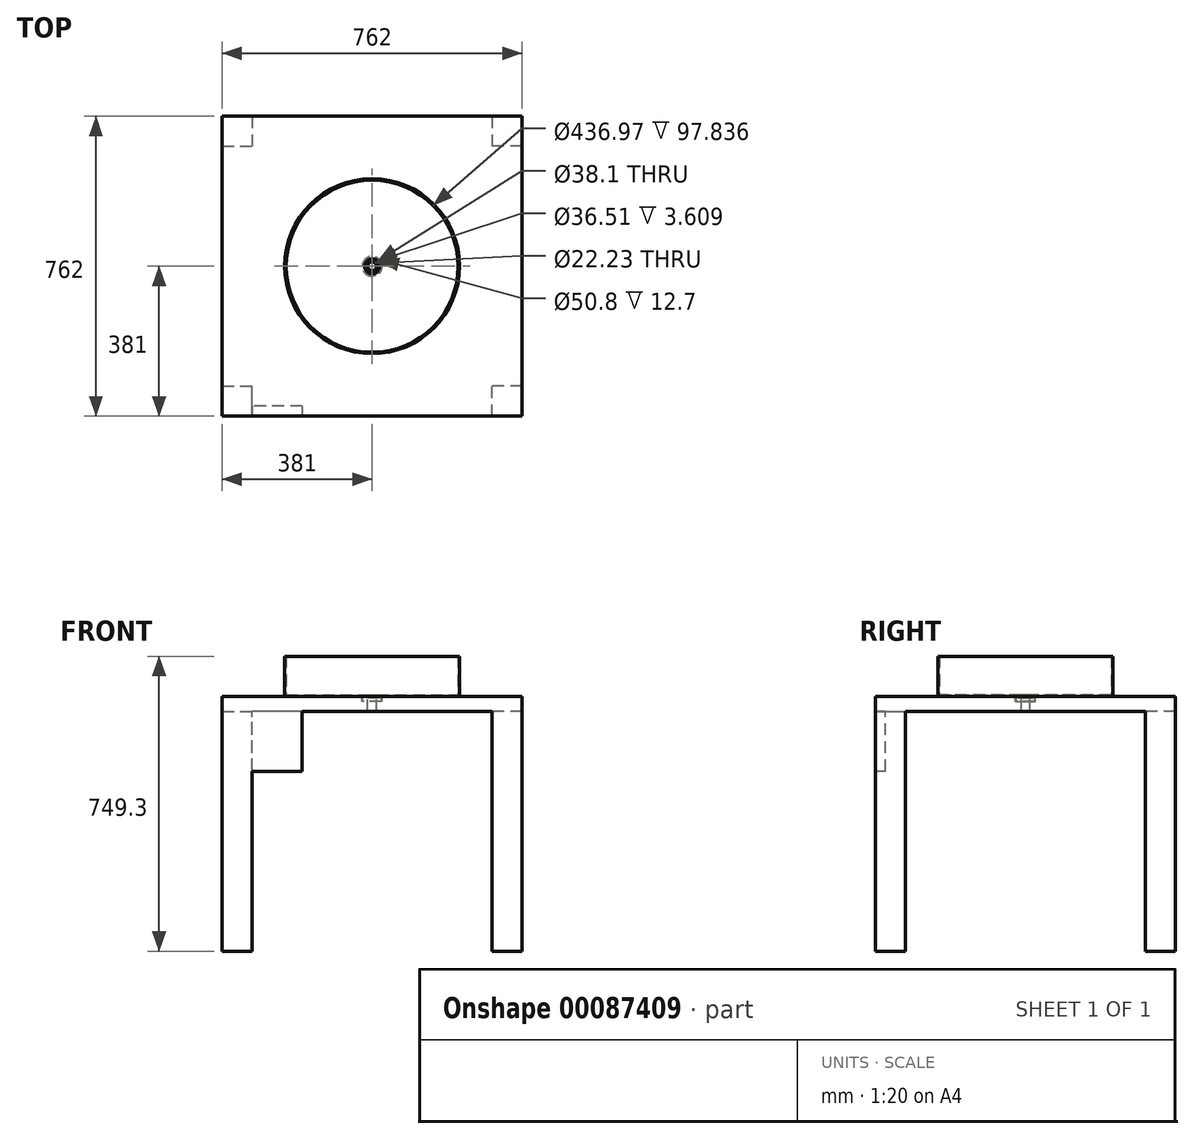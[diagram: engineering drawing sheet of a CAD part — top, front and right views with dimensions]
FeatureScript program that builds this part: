
annotation { "Feature Type Name" : "Feature", "Feature Type Description" : "" }
export const myFeature = defineFeature(function(context is Context, id is Id, definition is map)
    precondition{}
    {
        {
            var Q0;
            Q0=qCreatedBy(makeId("Top.planeOp"),FACE);
            var sketch = newSketch(context, id + "F0", { "sketchPlane" : qUnion([Q0])});
            skLineSegment(sketch, "E0.bottom", {"start": v(381, 381) * mm, "end": v(-381, 381) * mm});
            skLineSegment(sketch, "E0.top", {"start": v(381, -381) * mm, "end": v(-381, -381) * mm});
            skLineSegment(sketch, "E0.left", {"start": v(381, 381) * mm, "end": v(381, -381) * mm});
            skLineSegment(sketch, "E0.right", {"start": v(-381, 381) * mm, "end": v(-381, -381) * mm});
            skPoint(sketch, "E0.middle", {"position": v(0, 0) * mm});
            skSolve(sketch);
        }
        {
            var Q0;
            Q0 = qSketchRegion(id + "F0", true);
            extrude(context, id + "F1", {"entities" : qUnion([Q0]), "depth" : 38.1 * mm});
        }
        {
            var Q0;
            Q0=makeQuery(id+"F1.opExtrude","CAP_FACE",FACE,{"disambiguationData":[OSD([sQuery(id+"F0.wireOp",EDGE,"E0.bottom"),sQuery(id+"F0.wireOp",EDGE,"E0.top"),sQuery(id+"F0.wireOp",EDGE,"E0.left"),sQuery(id+"F0.wireOp",EDGE,"E0.right")])],"isStart":true});
            var sketch = newSketch(context, id + "F2", { "sketchPlane" : qUnion([Q0])});
            skLineSegment(sketch, "E1.bottom", {"start": v(-381, 381) * mm, "end": v(-304.8, 381) * mm});
            skLineSegment(sketch, "E1.top", {"start": v(-381, 304.8) * mm, "end": v(-304.8, 304.8) * mm});
            skLineSegment(sketch, "E1.left", {"start": v(-381, 381) * mm, "end": v(-381, 304.8) * mm});
            skLineSegment(sketch, "E1.right", {"start": v(-304.8, 381) * mm, "end": v(-304.8, 304.8) * mm});
            skLineSegment(sketch, "E2.bottom", {"start": v(381, 381) * mm, "end": v(304.8, 381) * mm});
            skLineSegment(sketch, "E2.top", {"start": v(381, 304.8) * mm, "end": v(304.8, 304.8) * mm});
            skLineSegment(sketch, "E2.left", {"start": v(381, 381) * mm, "end": v(381, 304.8) * mm});
            skLineSegment(sketch, "E2.right", {"start": v(304.8, 381) * mm, "end": v(304.8, 304.8) * mm});
            skLineSegment(sketch, "E3.bottom", {"start": v(381, -381) * mm, "end": v(304.8, -381) * mm});
            skLineSegment(sketch, "E3.top", {"start": v(381, -304.8) * mm, "end": v(304.8, -304.8) * mm});
            skLineSegment(sketch, "E3.left", {"start": v(381, -381) * mm, "end": v(381, -304.8) * mm});
            skLineSegment(sketch, "E3.right", {"start": v(304.8, -381) * mm, "end": v(304.8, -304.8) * mm});
            skLineSegment(sketch, "E4.bottom", {"start": v(-381, -381) * mm, "end": v(-304.8, -381) * mm});
            skLineSegment(sketch, "E4.top", {"start": v(-381, -304.8) * mm, "end": v(-304.8, -304.8) * mm});
            skLineSegment(sketch, "E4.left", {"start": v(-381, -381) * mm, "end": v(-381, -304.8) * mm});
            skLineSegment(sketch, "E4.right", {"start": v(-304.8, -381) * mm, "end": v(-304.8, -304.8) * mm});
            skSolve(sketch);
        }
        {
            var Q0;
            Q0 = qSketchRegion(id + "F2", true);
            extrude(context, id + "F3", {"entities" : qUnion([Q0]), "operationType" : NewBodyOperationType.ADD, "depth" : 609.6 * mm});
        }
        {
            var Q0;
            Q0=makeQuery(id+"F1.opExtrude","CAP_FACE",FACE,{"disambiguationData":[OSD([sQuery(id+"F0.wireOp",EDGE,"E0.bottom"),sQuery(id+"F0.wireOp",EDGE,"E0.top"),sQuery(id+"F0.wireOp",EDGE,"E0.left"),sQuery(id+"F0.wireOp",EDGE,"E0.right")])],"isStart":false});
            var sketch = newSketch(context, id + "F4", { "sketchPlane" : qUnion([Q0])});
            skCircle(sketch, "E5", {"center": v(0, 0) * mm, "radius": 18.26 * mm});
            skSolve(sketch);
        }
        {
            var Q0;
            Q0 = qSketchRegion(id + "F4", true);
            extrude(context, id + "F5", {"entities" : qUnion([Q0]), "operationType" : NewBodyOperationType.REMOVE, "oppositeDirection" : true, "depth" : 3.6 * mm});
        }
        {
            var Q0;
            Q0=makeQuery(id+"F5.boolean.opBoolean","COPY",FACE,{"derivedFrom":makeQuery(id+"F5.opExtrude","CAP_FACE",FACE,{"disambiguationData":[OSD([sQuery(id+"F4.wireOp",EDGE,"E5")])],"isStart":false})});
            var sketch = newSketch(context, id + "F6", { "sketchPlane" : qUnion([Q0])});
            skCircle(sketch, "E6", {"center": v(0, 0) * mm, "radius": 11.11 * mm});
            skSolve(sketch);
        }
        {
            var Q0;
            Q0 = qSketchRegion(id + "F6", true);
            extrude(context, id + "F7", {"entities" : qUnion([Q0]), "operationType" : NewBodyOperationType.REMOVE, "endBound" : BoundingType.THROUGH_ALL, "oppositeDirection" : true, "depth" : 25.4 * mm});
        }
        {
            var Q0;
            Q0=makeQuery(id+"F5.boolean.opBoolean","COPY",FACE,{"derivedFrom":makeQuery(id+"F5.opExtrude","CAP_FACE",FACE,{"disambiguationData":[OSD([sQuery(id+"F4.wireOp",EDGE,"E5")])],"isStart":false})});
            var sketch = newSketch(context, id + "F8", { "sketchPlane" : qUnion([Q0])});
            skCircle(sketch, "E7", {"center": v(0, 0) * mm, "radius": 12.7 * mm});
            skSolve(sketch);
        }
        {
            var Q0;
            Q0=makeQuery(id+"F1.opExtrude","CAP_FACE",FACE,{"disambiguationData":[OSD([sQuery(id+"F0.wireOp",EDGE,"E0.bottom"),sQuery(id+"F0.wireOp",EDGE,"E0.top"),sQuery(id+"F0.wireOp",EDGE,"E0.left"),sQuery(id+"F0.wireOp",EDGE,"E0.right")])],"isStart":false});
            var sketch = newSketch(context, id + "F9", { "sketchPlane" : qUnion([Q0])});
            skCircle(sketch, "E8", {"center": v(0, 0) * mm, "radius": 25.4 * mm});
            skCircle(sketch, "E9.0", {"center": v(0, 0) * mm, "radius": 23.81 * mm});
            skSolve(sketch);
        }
        {
            var Q0;
            Q0 = qSketchRegion(id + "F9", true);
            extrude(context, id + "F10", {"entities" : qUnion([Q0]), "operationType" : NewBodyOperationType.REMOVE, "oppositeDirection" : true, "depth" : 12.7 * mm});
        }
        {
            var Q0;
            Q0=makeQuery(id+"F3.boolean.opBoolean","MERGE",FACE,{"derivedFrom":[makeQuery(id+"F1.opExtrude","SWEPT_FACE",FACE,{"disambiguationData":[OSD([sQuery(id+"F0.wireOp",EDGE,"E0.top")])]}),makeQuery(id+"F3.opExtrude","SWEPT_FACE",FACE,{"disambiguationData":[OSD([sQuery(id+"F2.wireOp",EDGE,"E1.bottom")])]}),makeQuery(id+"F3.opExtrude","SWEPT_FACE",FACE,{"disambiguationData":[OSD([sQuery(id+"F2.wireOp",EDGE,"E2.bottom")])]})]});
            var sketch = newSketch(context, id + "F11", { "sketchPlane" : qUnion([Q0])});
            skLineSegment(sketch, "E10.bottom", {"start": v(-304.8, 0) * mm, "end": v(-177.8, 0) * mm});
            skLineSegment(sketch, "E10.top", {"start": v(-304.8, -152.4) * mm, "end": v(-177.8, -152.4) * mm});
            skLineSegment(sketch, "E10.left", {"start": v(-304.8, 0) * mm, "end": v(-304.8, -152.4) * mm});
            skLineSegment(sketch, "E10.right", {"start": v(-177.8, 0) * mm, "end": v(-177.8, -152.4) * mm});
            skSolve(sketch);
        }
        {
            var Q0;
            Q0 = qSketchRegion(id + "F11", true);
            extrude(context, id + "F12", {"entities" : qUnion([Q0]), "operationType" : NewBodyOperationType.ADD, "oppositeDirection" : true, "depth" : 25.4 * mm});
        }
        {
            var Q0;
            Q0=qCreatedBy(makeId("Front.planeOp"),FACE);
            var sketch = newSketch(context, id + "F13", { "sketchPlane" : qUnion([Q0])});
            skLineSegment(sketch, "E11", {"start": v(19.05, 38.1) * mm, "end": v(222.25, 38.1) * mm});
            skLineSegment(sketch, "E12", {"start": v(222.25, 38.1) * mm, "end": v(222.25, 139.7) * mm});
            skLineSegment(sketch, "E13.0", {"start": v(218.49, 41.86) * mm, "end": v(218.49, 139.7) * mm});
            skLineSegment(sketch, "E13.1", {"start": v(163.8, 41.86) * mm, "end": v(218.49, 41.86) * mm});
            skLineSegment(sketch, "E14", {"start": v(218.49, 139.7) * mm, "end": v(222.25, 139.7) * mm});
            skLineSegment(sketch, "E15", {"start": v(163.8, 41.86) * mm, "end": v(19.05, 41.86) * mm});
            skLineSegment(sketch, "E16", {"start": v(19.05, 38.1) * mm, "end": v(19.05, 41.86) * mm});
            skSolve(sketch);
        }
        {
            var Q0;
            Q0 = qSketchRegion(id + "F13", true);
            var Q1;
            Q1=sQuery(id+"F8.wireOp",EDGE,"E7");
            revolve(context, id + "F14", {"entities" : qUnion([Q0]), "axis" : qUnion([Q1]), "revolveType" : RevolveType.FULL});
        }
    });
